# Revit family: No interlocked sockets 250 V
name_source: partatom
category: Installations électriques
revit_build: Autodesk Revit 2018 (Build: 20170223_1515(x64)
units: mm (PartAtom-declared; Revit-internal decimal feet)

## family parameters
Conserver l'orientation des annotations = Non
Cote de connecteur circulaire = Utiliser le diamètre
Couper avec des vides une fois chargée = Non
Hôte = Face
Partagée = Non
Point de calcul de pièce = Non
Type d'élément = Normal

## types (9) — shared parameters
Elévation par défaut = 1000 mm  [stored 3.28084 ft]
Fabricant = Legrand
Flush E or Surface mounting S = flush mounting
International standard socket for flush mounting or surface mounting with accessory allows the connection of power devices = Socket for domestic use
Maximum use temperature = 40
Minimum use temperature = -25
Product family = 0854-P17 TEMPRA PRO
connecting type = screw terminals
depth for flush mounting mm = 26 mm
depth mm = 43 mm  [stored 0.141076 ft]
halogen free = Oui
intensity A = 16 A
material of box = plastic
protection class IP = IP54
resistance to chocks IK = 8
zero-valued in all types: Position of earth h

## per-type parameters (varying)
| type | Description | Number of poles | Standard IEC or NFC | Tension V | characteristic color | height mm | horizontal fixing distance mm | vertical fixing distance mm | width mm |
| LG-057676 - P17 - 250 V - 16 A - 2P+E | LG-057676_Panel mounting sockets P17  250 V - 16 A - 2P+E | 2 | SCHUKO |  | blue | 75 mm | 60 mm | 60 mm | 75 mm |
| LG-057675 - P17- 250 V - 16 A - 2P+E | LG-057675_Panel mounting sockets P17- 250 V - 16 A - 2P+E | 2 | SCHUKO |  | white | 62 mm | 38 mm | 38 mm | 50 mm  [stored 0.164042 ft] |
| LG-057674 - P17 - IP54 - 250 V - 16 A - 2P+E | LG-057674_Socket P17 - IP54 - 250 V - 16 A - 2P+E | 2 | SCHUKO |  | white | 62 mm | 38 mm | 38 mm | 50 mm  [stored 0.164042 ft] |
| LG-057673 - P17 - IP54 - 250 V - 16 A - 2P+E | LG-057673_Socket P17 - IP54 - 250 V - 16 A - 2P+E | 2 | SCHUKO |  | black | 62 mm | 38 mm | 38 mm | 50 mm  [stored 0.164042 ft] |
| LG-057672 - P17 - 250 V - 16 A - 2P+E | LG-057672_Panel mounting sockets P17  250 V - 16 A - 2P+E | 3 | SCHUKO | 230 V  50/60 Hz blue | blue | 75 mm | 60 mm | 60 mm | 75 mm |
| LG-057671 - P17 - IP54 - 250 V - 16 A - 2P+E | LG-057671_Socket P17 - IP54 - 250 V - 16 A - 2P+E | 3 | SCHUKO | 230 V  50/60 Hz blue | blue | 75 mm | 60 mm | 60 mm | 75 mm |
| LG-057670-  P17 - IP54 - 250 V - 16 A - 2P+E | LG-057670_Socket P17 IP54 - 250 V - 16 A - 2P+E | 3 | SCHUKO | 230 V  50/60 Hz blue | blue | 50 mm  [stored 0.164042 ft] | 38 mm | 38 mm | 50 mm  [stored 0.164042 ft] |
| LG-057669 - P17 - 250 V - 16 A - 2P+E | LG-057669_Panel mounting sockets P17 - 250 V - 16 A - 2P+E | 3 | SCHUKO | 230 V  50/60 Hz blue | white | 50 mm  [stored 0.164042 ft] | 38 mm | 38 mm | 50 mm  [stored 0.164042 ft] |
| LG-057667 - P17 - IP54 - 250 V - 16 A - 2P+E | LG-057667_Socket P17 - IP54 - 250 V - 16 A - 2P+E | 3 | NFC | 230 V  50/60 Hz blue | blue | 50 mm  [stored 0.164042 ft] | 38 mm | 38 mm | 50 mm  [stored 0.164042 ft] |

note: [stored X ft] marks values corroborated as IEEE doubles in the binary element streams (Revit-internal decimal feet)
